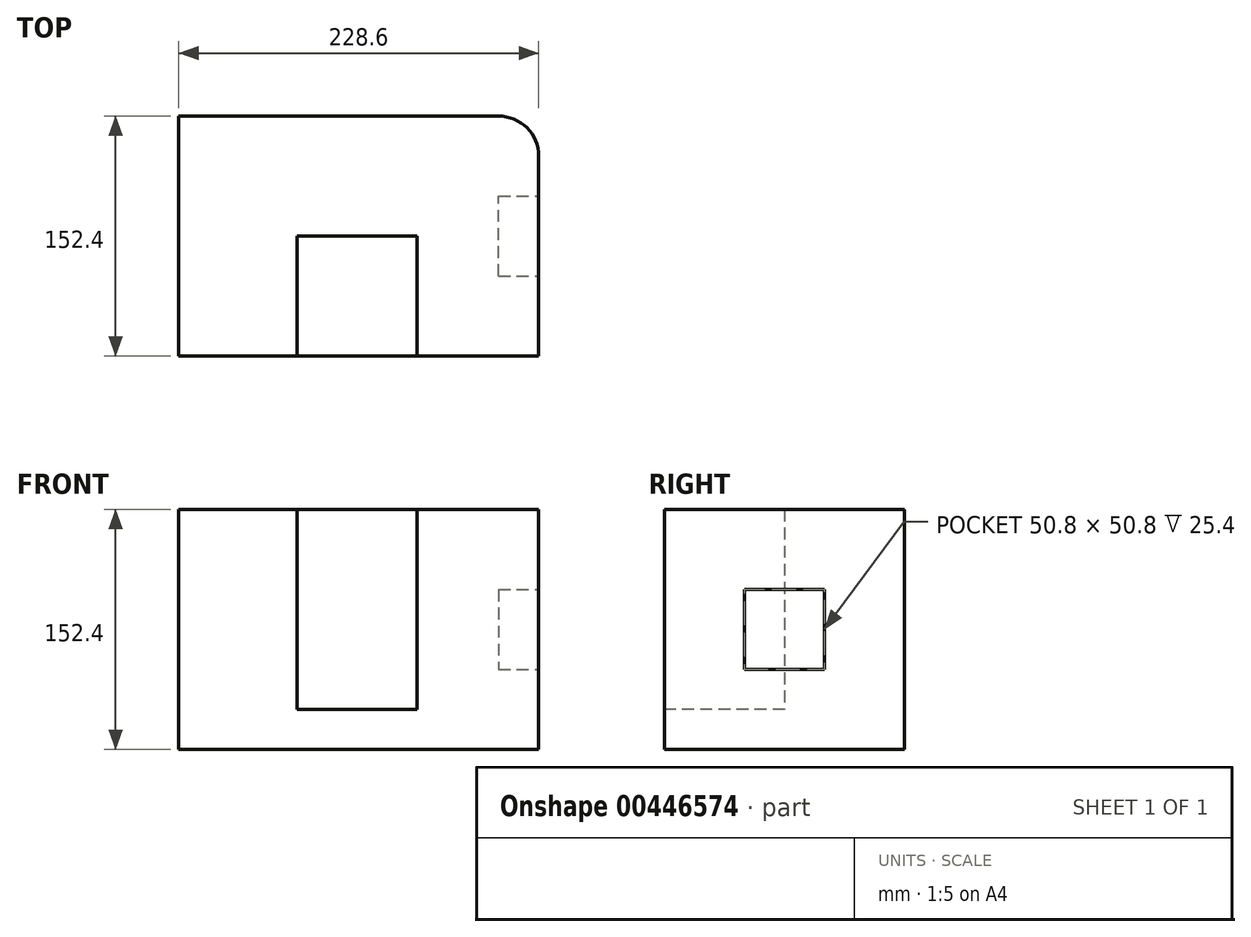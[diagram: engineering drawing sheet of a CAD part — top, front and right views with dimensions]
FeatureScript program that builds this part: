
annotation { "Feature Type Name" : "Feature", "Feature Type Description" : "" }
export const myFeature = defineFeature(function(context is Context, id is Id, definition is map)
    precondition{}
    {
        {
            var Q0;
            Q0=qCreatedBy(makeId("Front.planeOp"),FACE);
            var sketch = newSketch(context, id + "F0", { "sketchPlane" : qUnion([Q0])});
            skLineSegment(sketch, "E0.bottom", {"start": v(-114.3, 76.2) * mm, "end": v(114.3, 76.2) * mm});
            skLineSegment(sketch, "E0.top", {"start": v(-114.3, -76.2) * mm, "end": v(114.3, -76.2) * mm});
            skLineSegment(sketch, "E0.left", {"start": v(-114.3, 76.2) * mm, "end": v(-114.3, -76.2) * mm});
            skLineSegment(sketch, "E0.right", {"start": v(114.3, 76.2) * mm, "end": v(114.3, -76.2) * mm});
            skSolve(sketch);
        }
        {
            var Q0;
            Q0=makeQuery(id+"F0.imprint","IMPRINT",FACE,{"disambiguationData":[TD([[makeQuery(id+"F0.imprint","IMPRINT",EDGE,{"derivedFrom":sQuery(id+"F0.wireOp",EDGE,"E0.bottom")}),-1.0]])]});
            extrude(context, id + "F1", {"entities" : qUnion([Q0]), "endBound" : BoundingType.SYMMETRIC, "depth" : 152.4 * mm});
        }
        {
            var Q0;
            Q0=makeQuery(id+"F1.opExtrude","CAP_FACE",FACE,{"disambiguationData":[OSD([sQuery(id+"F0.wireOp",EDGE,"E0.bottom"),sQuery(id+"F0.wireOp",EDGE,"E0.top"),sQuery(id+"F0.wireOp",EDGE,"E0.left"),sQuery(id+"F0.wireOp",EDGE,"E0.right")])],"isStart":false});
            var sketch = newSketch(context, id + "F2", { "sketchPlane" : qUnion([Q0])});
            skLineSegment(sketch, "E1.bottom", {"start": v(-39.13, 76.2) * mm, "end": v(37.07, 76.2) * mm});
            skLineSegment(sketch, "E1.top", {"start": v(-39.13, -50.8) * mm, "end": v(37.07, -50.8) * mm});
            skLineSegment(sketch, "E1.left", {"start": v(-39.13, 76.2) * mm, "end": v(-39.13, -50.8) * mm});
            skLineSegment(sketch, "E1.right", {"start": v(37.07, 76.2) * mm, "end": v(37.07, -50.8) * mm});
            skSolve(sketch);
        }
        {
            var Q0;
            Q0=makeQuery(id+"F2.imprint","IMPRINT",FACE,{"disambiguationData":[TD([[makeQuery(id+"F2.imprint","IMPRINT",EDGE,{"derivedFrom":sQuery(id+"F2.wireOp",EDGE,"E1.bottom")}),-1.0]])]});
            extrude(context, id + "F3", {"entities" : qUnion([Q0]), "operationType" : NewBodyOperationType.REMOVE, "oppositeDirection" : true, "depth" : 76.2 * mm});
        }
        {
            var Q0;
            Q0=makeQuery(id+"F1.opExtrude","CAP_EDGE",EDGE,{"disambiguationData":[OSD([sQuery(id+"F0.wireOp",EDGE,"E0.right")])],"isStart":true});
            fillet(context, id + "F4", {"entities" : qUnion([Q0]), "radius" : 25.4 * mm, "tangentPropagation" : true, "allowEdgeOverflow" : false});
        }
        {
            var Q0;
            Q0=makeQuery(id+"F1.opExtrude","SWEPT_FACE",FACE,{"disambiguationData":[OSD([sQuery(id+"F0.wireOp",EDGE,"E0.right")])]});
            var sketch = newSketch(context, id + "F5", { "sketchPlane" : qUnion([Q0])});
            skLineSegment(sketch, "E2.bottom", {"start": v(-25.4, 25.4) * mm, "end": v(25.4, 25.4) * mm});
            skLineSegment(sketch, "E2.top", {"start": v(-25.4, -25.4) * mm, "end": v(25.4, -25.4) * mm});
            skLineSegment(sketch, "E2.left", {"start": v(-25.4, 25.4) * mm, "end": v(-25.4, -25.4) * mm});
            skLineSegment(sketch, "E2.right", {"start": v(25.4, 25.4) * mm, "end": v(25.4, -25.4) * mm});
            skSolve(sketch);
        }
        {
            var Q0;
            Q0=makeQuery(id+"F5.imprint","IMPRINT",FACE,{"disambiguationData":[TD([[makeQuery(id+"F5.imprint","IMPRINT",EDGE,{"derivedFrom":sQuery(id+"F5.wireOp",EDGE,"E2.bottom")}),-1.0]])]});
            extrude(context, id + "F6", {"entities" : qUnion([Q0]), "operationType" : NewBodyOperationType.REMOVE, "oppositeDirection" : true, "depth" : 25.4 * mm});
        }
    });
